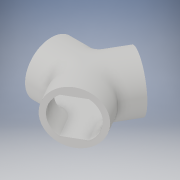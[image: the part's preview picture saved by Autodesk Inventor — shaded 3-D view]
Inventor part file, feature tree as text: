
AUTODESK INVENTOR PART (.ipt)
format: ipt  version: 2017 (Build 210142000, 142)  size: 243,200 bytes
history: native  units: in
note: dims shown in document units (in); Inventor stores cm internally (conversion verified against a paired STEP export)
features: sketch x4, extrude x2, other x2, pattern_circular x2, sweep x1, mirror x1
ambient origin geometry x8: Origin, YZ Plane, XZ Plane, XY Plane, X Axis, Y Axis, Z Axis, Center Point
bodies: Solid1 (feature_tree)
feature tree (12):
  extrude  "corridor"  Depth=6.6667in TaperAngle=0.0deg
  other  "found rotaion axis"
  other  "rotaion axis"
  pattern_circular  "other corridors"  Count=3 Angle=360.0deg
  sweep  "curve edjes"
  pattern_circular  "repeat curve edjes"  [2 undecoded]
  extrude  "bottom hole fill up"  [1 undecoded]
  mirror  "top hole fill up"
  sketch  "Sketch1"  dims[d10=6.6667in d11=4.0in d12=4.0in d13=0.0in]
  sketch  "Sketch4"  dims[d14=9.7746in]
  sketch  "Sketch5"  dims[d15=2.8217in d16=1.1811in d17=360.0deg]
  sketch  "Sketch7"  dims[d24=0.0in d25=0.0in d26=1.1811in d27=360.0deg d37=1.554in d38=0.0in]
note: 3 required parameter values undecoded (feature->parameter linkage not recoverable at this tier; creation-order binding heuristic only, values carry confidence <= 0.55)
